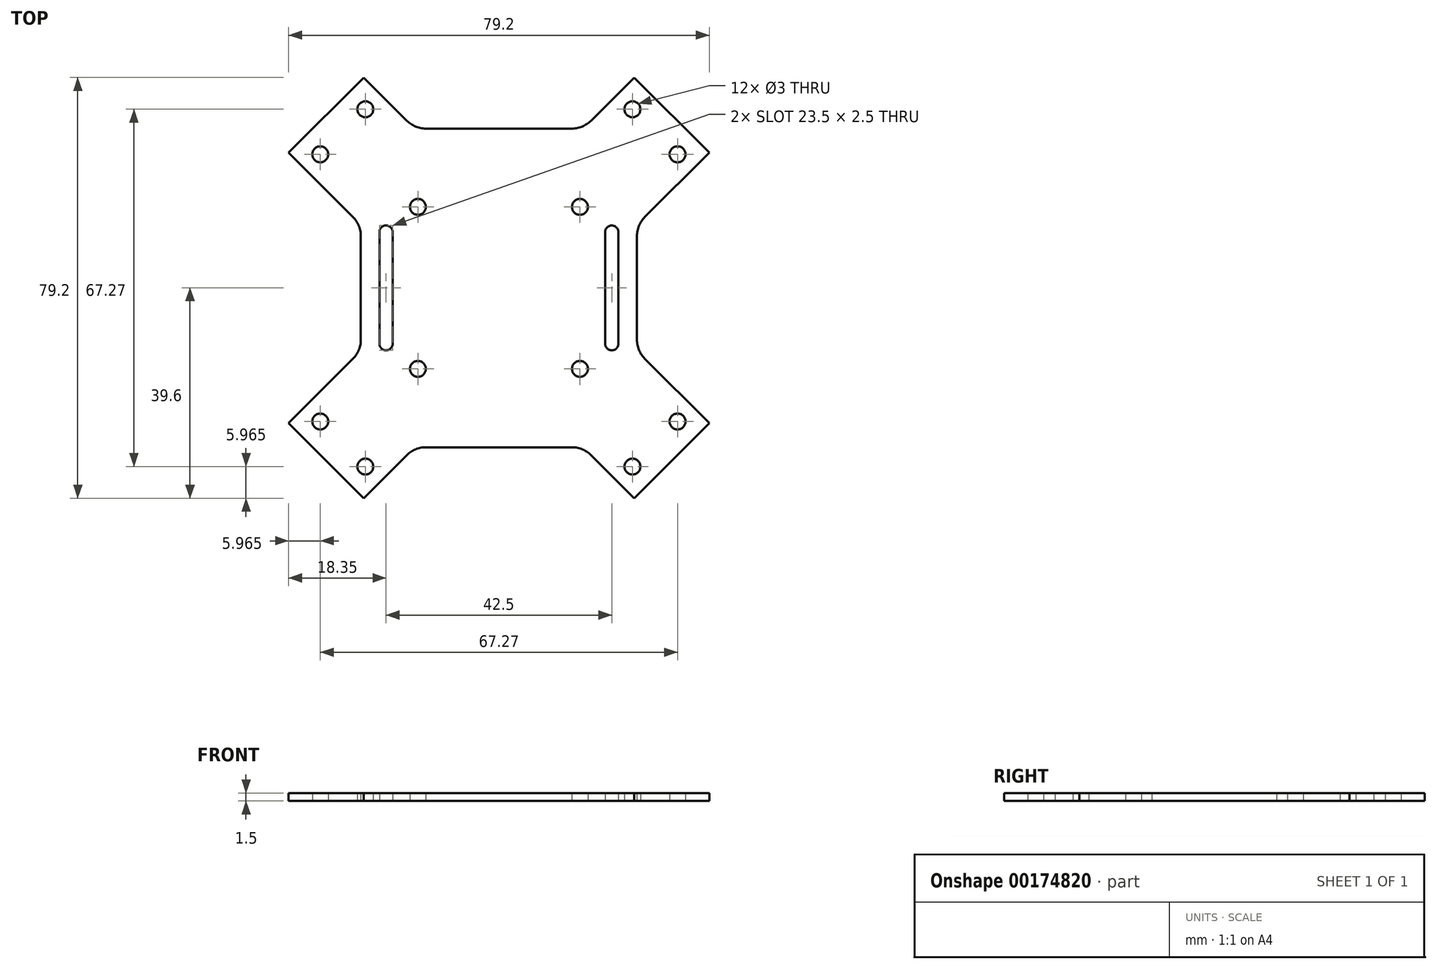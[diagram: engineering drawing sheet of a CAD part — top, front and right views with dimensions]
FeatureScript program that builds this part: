
annotation { "Feature Type Name" : "Feature", "Feature Type Description" : "" }
export const myFeature = defineFeature(function(context is Context, id is Id, definition is map)
    precondition{}
    {
        {
            var Q0;
            Q0=qCreatedBy(makeId("Top.planeOp"),FACE);
            var sketch = newSketch(context, id + "F0", { "sketchPlane" : qUnion([Q0])});
            skLineSegment(sketch, "E0.bottom", {"start": v(-15.25, 15.25) * mm, "end": v(15.25, 15.25) * mm, "construction": true});
            skLineSegment(sketch, "E0.top", {"start": v(-15.25, -15.25) * mm, "end": v(15.25, -15.25) * mm, "construction": true});
            skLineSegment(sketch, "E0.left", {"start": v(-15.25, 15.25) * mm, "end": v(-15.25, -15.25) * mm, "construction": true});
            skLineSegment(sketch, "E0.right", {"start": v(15.25, 15.25) * mm, "end": v(15.25, -15.25) * mm, "construction": true});
            skLineSegment(sketch, "E1", {"start": v(0, 0) * mm, "end": v(-70.71, 70.71) * mm, "construction": true});
            skLineSegment(sketch, "E2", {"start": v(0, 0) * mm, "end": v(70.71, 70.71) * mm, "construction": true});
            skLineSegment(sketch, "E3", {"start": v(0, 0) * mm, "end": v(70.71, -70.71) * mm, "construction": true});
            skLineSegment(sketch, "E4", {"start": v(0, 0) * mm, "end": v(-70.71, -70.71) * mm, "construction": true});
            skCircle(sketch, "E5", {"center": v(70.71, 70.71) * mm, "radius": 63.5 * mm, "construction": true});
            skCircle(sketch, "E6", {"center": v(-70.71, 70.71) * mm, "radius": 63.5 * mm, "construction": true});
            skCircle(sketch, "E7", {"center": v(-70.71, -70.71) * mm, "radius": 63.5 * mm, "construction": true});
            skCircle(sketch, "E8", {"center": v(70.71, -70.71) * mm, "radius": 63.5 * mm, "construction": true});
            skCircle(sketch, "E9", {"center": v(0, 0) * mm, "radius": 100 * mm, "construction": true});
            skCircle(sketch, "E10", {"center": v(-15.25, 15.25) * mm, "radius": 1.5 * mm});
            skCircle(sketch, "E11", {"center": v(-15.25, -15.25) * mm, "radius": 1.5 * mm});
            skCircle(sketch, "E12", {"center": v(15.25, -15.25) * mm, "radius": 1.5 * mm});
            skCircle(sketch, "E13", {"center": v(15.25, 15.25) * mm, "radius": 1.5 * mm});
            skLineSegment(sketch, "E14", {"start": v(-39.6, 25.46) * mm, "end": v(-25.46, 39.6) * mm});
            skLineSegment(sketch, "E15", {"start": v(-25.46, 39.6) * mm, "end": v(-15.86, 30) * mm});
            skLineSegment(sketch, "E16", {"start": v(39.6, -25.46) * mm, "end": v(25.46, -39.6) * mm});
            skLineSegment(sketch, "E17", {"start": v(25.46, -39.6) * mm, "end": v(15.86, -30) * mm});
            skLineSegment(sketch, "E18", {"start": v(-39.6, -25.46) * mm, "end": v(-26, -11.86) * mm});
            skLineSegment(sketch, "E19", {"start": v(25.46, 39.6) * mm, "end": v(39.6, 25.46) * mm});
            skLineSegment(sketch, "E20", {"start": v(39.6, 25.46) * mm, "end": v(26, 11.86) * mm});
            skLineSegment(sketch, "E21", {"start": v(-25.46, -39.6) * mm, "end": v(-39.6, -25.46) * mm});
            skLineSegment(sketch, "E22.trimOffspring", {"start": v(15.86, 30) * mm, "end": v(25.46, 39.6) * mm});
            skLineSegment(sketch, "E23.trimOffspring", {"start": v(-15.86, -30) * mm, "end": v(-25.46, -39.6) * mm});
            skLineSegment(sketch, "E24.trimOffspring", {"start": v(-26, 11.86) * mm, "end": v(-39.6, 25.46) * mm});
            skLineSegment(sketch, "E25.trimOffspring", {"start": v(26, -11.86) * mm, "end": v(39.6, -25.46) * mm});
            skLineSegment(sketch, "E26", {"start": v(-20, 10.5) * mm, "end": v(-20, -10.5) * mm});
            skLineSegment(sketch, "E27", {"start": v(20, 10.5) * mm, "end": v(20, -10.5) * mm});
            skLineSegment(sketch, "E28", {"start": v(-15.86, -30) * mm, "end": v(15.86, -30) * mm});
            skLineSegment(sketch, "E29", {"start": v(-15.86, 30) * mm, "end": v(15.86, 30) * mm});
            skCircle(sketch, "E30", {"center": v(25.15, 33.63) * mm, "radius": 1.5 * mm});
            skCircle(sketch, "E31", {"center": v(33.63, 25.15) * mm, "radius": 1.5 * mm});
            skCircle(sketch, "E32", {"center": v(-25.15, 33.63) * mm, "radius": 1.5 * mm});
            skCircle(sketch, "E33", {"center": v(-33.63, 25.15) * mm, "radius": 1.5 * mm});
            skCircle(sketch, "E34", {"center": v(-33.63, -25.15) * mm, "radius": 1.5 * mm});
            skCircle(sketch, "E35", {"center": v(-25.15, -33.63) * mm, "radius": 1.5 * mm});
            skCircle(sketch, "E36", {"center": v(25.15, -33.63) * mm, "radius": 1.5 * mm});
            skCircle(sketch, "E37", {"center": v(33.63, -25.15) * mm, "radius": 1.5 * mm});
            skLineSegment(sketch, "E38", {"start": v(-33.63, 25.15) * mm, "end": v(-25.15, 33.63) * mm, "construction": true});
            skLineSegment(sketch, "E39", {"start": v(25.15, 33.63) * mm, "end": v(33.63, 25.15) * mm, "construction": true});
            skLineSegment(sketch, "E40", {"start": v(33.63, -25.15) * mm, "end": v(25.15, -33.63) * mm, "construction": true});
            skLineSegment(sketch, "E41", {"start": v(-33.63, -25.15) * mm, "end": v(-25.15, -33.63) * mm, "construction": true});
            skArc(sketch, "E42", {"start": v(-20, 10.5) * mm, "mid": v(-21.25, 11.75) * mm, "end": v(-22.5, 10.5) * mm});
            skArc(sketch, "E43", {"start": v(-22.5, -10.5) * mm, "mid": v(-21.25, -11.75) * mm, "end": v(-20, -10.5) * mm});
            skLineSegment(sketch, "E44", {"start": v(-22.5, 10.5) * mm, "end": v(-22.5, -10.5) * mm});
            skLineSegment(sketch, "E45", {"start": v(-26, 11.86) * mm, "end": v(-26, -11.86) * mm});
            skLineSegment(sketch, "E46", {"start": v(26, 11.86) * mm, "end": v(26, -11.86) * mm});
            skArc(sketch, "E47", {"start": v(22.5, 10.5) * mm, "mid": v(21.25, 11.75) * mm, "end": v(20, 10.5) * mm});
            skArc(sketch, "E48", {"start": v(20, -10.5) * mm, "mid": v(21.25, -11.75) * mm, "end": v(22.5, -10.5) * mm});
            skLineSegment(sketch, "E49", {"start": v(22.5, 10.5) * mm, "end": v(22.5, -10.5) * mm});
            skSolve(sketch);
        }
        {
            var Q0;
            Q0 = qSketchRegion(id + "F0", true);
            extrude(context, id + "F1", {"entities" : qUnion([Q0]), "depth" : 1.5 * mm});
        }
        {
            var Q0;
            Q0=makeQuery(id+"F1.opExtrude","SWEPT_EDGE",EDGE,{"disambiguationData":[OSD([sQuery(id+"F0.wireOp",EDGE,"E15"),sQuery(id+"F0.wireOp",EDGE,"E29")])]});
            var Q1;
            Q1=makeQuery(id+"F1.opExtrude","SWEPT_EDGE",EDGE,{"disambiguationData":[OSD([sQuery(id+"F0.wireOp",EDGE,"E22.trimOffspring"),sQuery(id+"F0.wireOp",EDGE,"E29")])]});
            var Q2;
            Q2=makeQuery(id+"F1.opExtrude","SWEPT_EDGE",EDGE,{"disambiguationData":[OSD([sQuery(id+"F0.wireOp",EDGE,"E20"),sQuery(id+"F0.wireOp",EDGE,"E46")])]});
            var Q3;
            Q3=makeQuery(id+"F1.opExtrude","SWEPT_EDGE",EDGE,{"disambiguationData":[OSD([sQuery(id+"F0.wireOp",EDGE,"E25.trimOffspring"),sQuery(id+"F0.wireOp",EDGE,"E46")])]});
            var Q4;
            Q4=makeQuery(id+"F1.opExtrude","SWEPT_EDGE",EDGE,{"disambiguationData":[OSD([sQuery(id+"F0.wireOp",EDGE,"E18"),sQuery(id+"F0.wireOp",EDGE,"E45")])]});
            var Q5;
            Q5=makeQuery(id+"F1.opExtrude","SWEPT_EDGE",EDGE,{"disambiguationData":[OSD([sQuery(id+"F0.wireOp",EDGE,"E24.trimOffspring"),sQuery(id+"F0.wireOp",EDGE,"E45")])]});
            var Q6;
            Q6=makeQuery(id+"F1.opExtrude","SWEPT_EDGE",EDGE,{"disambiguationData":[OSD([sQuery(id+"F0.wireOp",EDGE,"E23.trimOffspring"),sQuery(id+"F0.wireOp",EDGE,"E28")])]});
            var Q7;
            Q7=makeQuery(id+"F1.opExtrude","SWEPT_EDGE",EDGE,{"disambiguationData":[OSD([sQuery(id+"F0.wireOp",EDGE,"E17"),sQuery(id+"F0.wireOp",EDGE,"E28")])]});
            fillet(context, id + "F2", {"entities" : qUnion([Q0, Q1, Q2, Q3, Q4, Q5, Q6, Q7]), "radius" : 5 * mm, "tangentPropagation" : true, "allowEdgeOverflow" : false});
        }
    });
